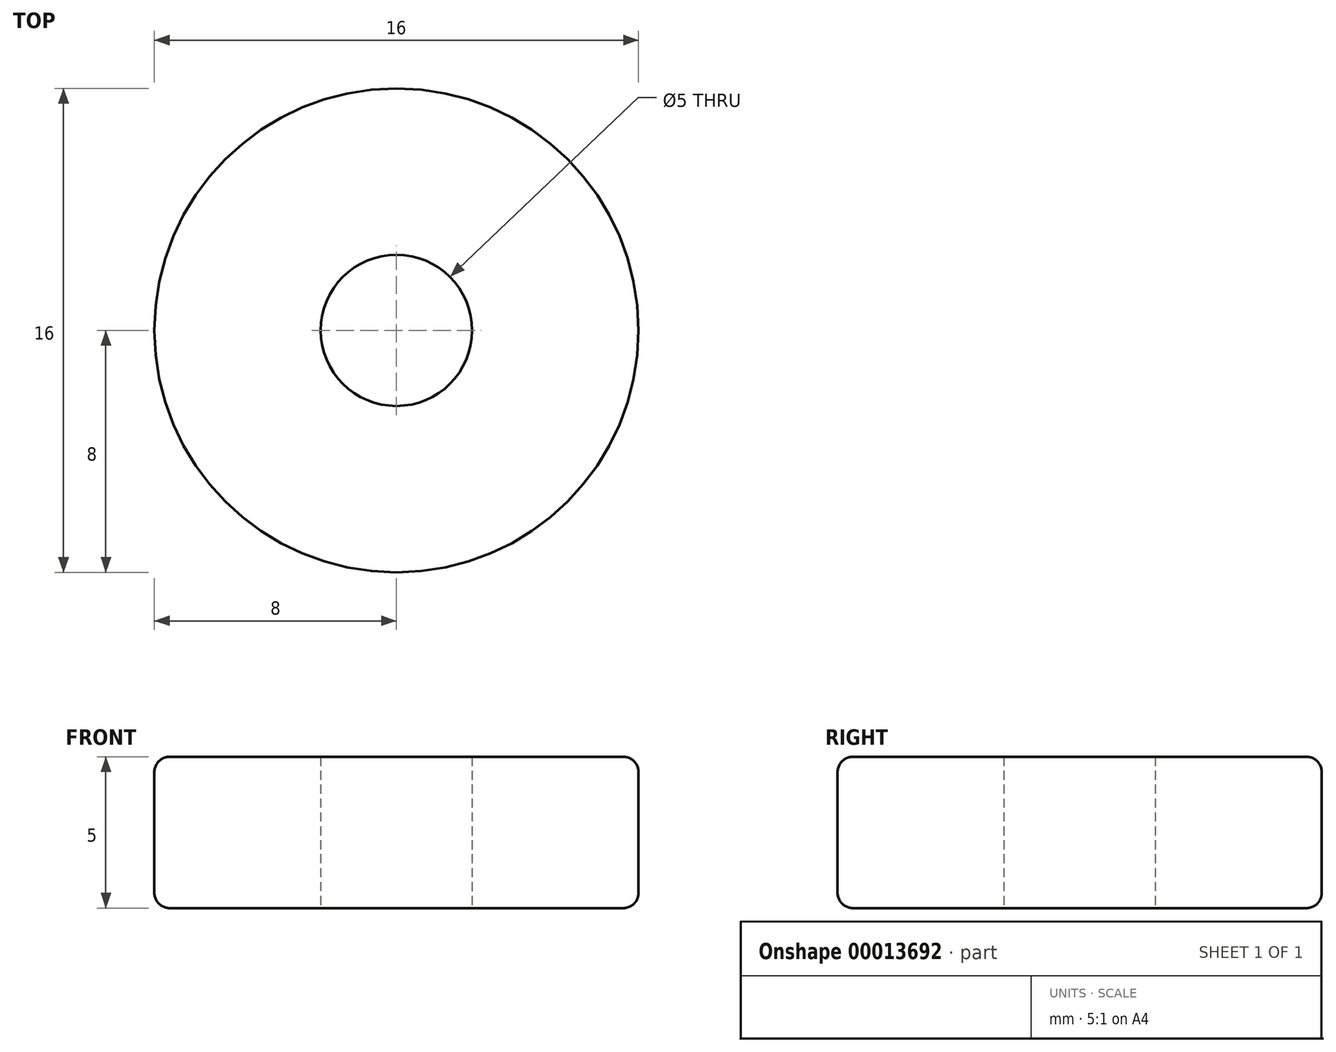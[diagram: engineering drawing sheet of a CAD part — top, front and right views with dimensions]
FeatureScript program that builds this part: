
annotation { "Feature Type Name" : "Feature", "Feature Type Description" : "" }
export const myFeature = defineFeature(function(context is Context, id is Id, definition is map)
    precondition{}
    {
        {
            var Q0;
            Q0=qCreatedBy(makeId("Top.planeOp"),FACE);
            var sketch = newSketch(context, id + "F0", { "sketchPlane" : qUnion([Q0])});
            skCircle(sketch, "E0", {"center": v(0, 0) * mm, "radius": 8 * mm});
            skCircle(sketch, "E1", {"center": v(0, 0) * mm, "radius": 2.5 * mm});
            skSolve(sketch);
        }
        {
            var Q0;
            Q0=makeQuery(id+"F0.imprint","IMPRINT",FACE,{"disambiguationData":[TD([[makeQuery(id+"F0.imprint","IMPRINT",EDGE,{"derivedFrom":sQuery(id+"F0.wireOp",EDGE,"E0")}),1.0]])]});
            extrude(context, id + "F1", {"entities" : qUnion([Q0]), "depth" : 5 * mm});
        }
        {
            var Q0;
            Q0=makeQuery(id+"F1.opExtrude","CAP_EDGE",EDGE,{"disambiguationData":[OSD([sQuery(id+"F0.wireOp",EDGE,"E0")])],"isStart":false});
            var Q1;
            Q1=makeQuery(id+"F1.opExtrude","CAP_EDGE",EDGE,{"disambiguationData":[OSD([sQuery(id+"F0.wireOp",EDGE,"E0")])],"isStart":true});
            fillet(context, id + "F2", {"entities" : qUnion([Q0, Q1]), "radius" : 0.5 * mm, "tangentPropagation" : true, "allowEdgeOverflow" : false});
        }
    });
